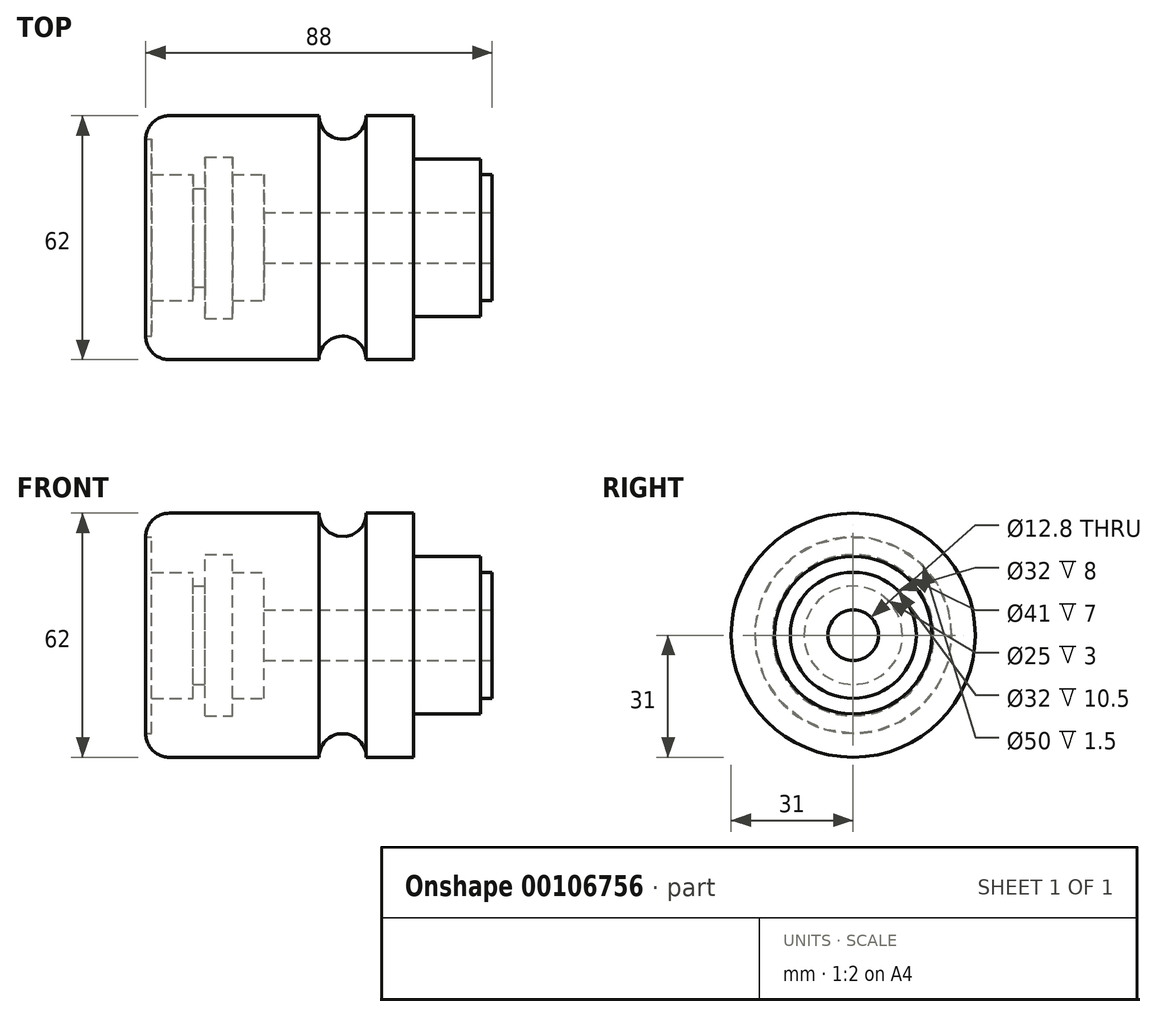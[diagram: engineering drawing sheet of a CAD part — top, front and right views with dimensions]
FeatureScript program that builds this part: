
annotation { "Feature Type Name" : "Feature", "Feature Type Description" : "" }
export const myFeature = defineFeature(function(context is Context, id is Id, definition is map)
    precondition{}
    {
        {
            var Q0;
            Q0=qCreatedBy(makeId("Front.planeOp"),FACE);
            var sketch = newSketch(context, id + "F0", { "sketchPlane" : qUnion([Q0])});
            skLineSegment(sketch, "E0", {"start": v(0, 0) * mm, "end": v(88, 0) * mm, "construction": true});
            skLineSegment(sketch, "E1.bottom", {"start": v(88, 0) * mm, "end": v(85, 0) * mm});
            skLineSegment(sketch, "E1.top", {"start": v(88, 16) * mm, "end": v(85, 16) * mm});
            skLineSegment(sketch, "E1.left", {"start": v(88, 0) * mm, "end": v(88, 16) * mm});
            skLineSegment(sketch, "E1.right", {"start": v(85, 0) * mm, "end": v(85, 16) * mm});
            skLineSegment(sketch, "E2.bottom", {"start": v(85, 0) * mm, "end": v(68, 0) * mm});
            skLineSegment(sketch, "E2.top", {"start": v(85, 20) * mm, "end": v(68, 20) * mm});
            skLineSegment(sketch, "E2.left", {"start": v(85, 0) * mm, "end": v(85, 20) * mm});
            skLineSegment(sketch, "E2.right", {"start": v(68, 0) * mm, "end": v(68, 20) * mm});
            skLineSegment(sketch, "E3.bottom", {"start": v(68, 0) * mm, "end": v(56, 0) * mm});
            skLineSegment(sketch, "E3.top", {"start": v(68, 31) * mm, "end": v(56, 31) * mm});
            skLineSegment(sketch, "E3.left", {"start": v(68, 0) * mm, "end": v(68, 31) * mm});
            skLineSegment(sketch, "E3.right", {"start": v(56, 0) * mm, "end": v(56, 31) * mm});
            skLineSegment(sketch, "E4.bottom", {"start": v(56, 0) * mm, "end": v(0, 0) * mm});
            skLineSegment(sketch, "E4.top", {"start": v(56, 31) * mm, "end": v(6, 31) * mm});
            skLineSegment(sketch, "E4.right", {"start": v(0, 0) * mm, "end": v(0, 25) * mm});
            skPoint(sketch, "E5.visualSharp", {"position": v(0, 31) * mm});
            skArc(sketch, "E5.filletArc", {"start": v(6, 31) * mm, "mid": v(1.76, 29.24) * mm, "end": v(0, 25) * mm});
            skLineSegment(sketch, "E6", {"start": v(44, 31) * mm, "end": v(44, 0) * mm});
            skArc(sketch, "E7", {"start": v(44, 31) * mm, "mid": v(50, 25) * mm, "end": v(56, 31) * mm});
            skSolve(sketch);
        }
        {
            var Q0;
            {var subQ1=sQuery(id+"F0.wireOp",EDGE,"E4.right");Q0=makeQuery(id+"F0.imprint","IMPRINT",FACE,{"disambiguationData":[TD([[makeQuery(id+"F0.imprint","IMPRINT",EDGE,{"derivedFrom":subQ1}),-1.0]])]});}
            var Q1;
            {var subQ0=sQuery(id+"F0.wireOp",EDGE,"E3.right");Q1=makeQuery(id+"F0.imprint","IMPRINT",FACE,{"disambiguationData":[TD([[makeQuery(id+"F0.imprint","IMPRINT",EDGE,{"derivedFrom":subQ0}),1.0]])]});}
            var Q2;
            {var subQ3=sQuery(id+"F0.wireOp",EDGE,"E3.bottom");Q2=makeQuery(id+"F0.imprint","IMPRINT",FACE,{"disambiguationData":[TD([[makeQuery(id+"F0.imprint","IMPRINT",EDGE,{"derivedFrom":subQ3}),-1.0]])]});}
            var Q3;
            {var subQ3=sQuery(id+"F0.wireOp",EDGE,"E2.bottom");Q3=makeQuery(id+"F0.imprint","IMPRINT",FACE,{"disambiguationData":[TD([[makeQuery(id+"F0.imprint","IMPRINT",EDGE,{"derivedFrom":subQ3}),-1.0]])]});}
            var Q4;
            {var subQ0=sQuery(id+"F0.wireOp",EDGE,"E1.bottom");Q4=makeQuery(id+"F0.imprint","IMPRINT",FACE,{"disambiguationData":[TD([[makeQuery(id+"F0.imprint","IMPRINT",EDGE,{"derivedFrom":subQ0}),-1.0]])]});}
            var Q5;
            Q5=sQuery(id+"F0.wireOp",EDGE,"E4.bottom");
            revolve(context, id + "F1", {"entities" : qUnion([Q0, Q1, Q2, Q3, Q4]), "axis" : qUnion([Q5]), "revolveType" : RevolveType.FULL});
        }
        {
            var Q0;
            Q0=qCreatedBy(makeId("Front.planeOp"),FACE);
            var sketch = newSketch(context, id + "F2", { "sketchPlane" : qUnion([Q0])});
            skLineSegment(sketch, "E8", {"start": v(0, 0) * mm, "end": v(149.16, 0) * mm, "construction": true});
            skLineSegment(sketch, "E9.bottom", {"start": v(88, 0) * mm, "end": v(30, 0) * mm});
            skLineSegment(sketch, "E9.top", {"start": v(88, 6.4) * mm, "end": v(30, 6.4) * mm});
            skLineSegment(sketch, "E9.left", {"start": v(88, 0) * mm, "end": v(88, 6.4) * mm});
            skLineSegment(sketch, "E9.right", {"start": v(30, 0) * mm, "end": v(30, 6.4) * mm});
            skLineSegment(sketch, "E10.bottom", {"start": v(30, 0) * mm, "end": v(22, 0) * mm});
            skLineSegment(sketch, "E10.top", {"start": v(30, 16) * mm, "end": v(22, 16) * mm});
            skLineSegment(sketch, "E10.left", {"start": v(30, 0) * mm, "end": v(30, 16) * mm});
            skLineSegment(sketch, "E10.right", {"start": v(22, 0) * mm, "end": v(22, 16) * mm});
            skLineSegment(sketch, "E11.bottom", {"start": v(22, 0) * mm, "end": v(15, 0) * mm});
            skLineSegment(sketch, "E11.top", {"start": v(22, 20.5) * mm, "end": v(15, 20.5) * mm});
            skLineSegment(sketch, "E11.left", {"start": v(22, 0) * mm, "end": v(22, 20.5) * mm});
            skLineSegment(sketch, "E11.right", {"start": v(15, 0) * mm, "end": v(15, 20.5) * mm});
            skLineSegment(sketch, "E12.bottom", {"start": v(15, 0) * mm, "end": v(12, 0) * mm});
            skLineSegment(sketch, "E12.top", {"start": v(15, 12.5) * mm, "end": v(12, 12.5) * mm});
            skLineSegment(sketch, "E12.left", {"start": v(15, 0) * mm, "end": v(15, 12.5) * mm});
            skLineSegment(sketch, "E12.right", {"start": v(12, 0) * mm, "end": v(12, 12.5) * mm});
            skLineSegment(sketch, "E13.bottom", {"start": v(12, 0) * mm, "end": v(1.5, 0) * mm});
            skLineSegment(sketch, "E13.top", {"start": v(12, 16) * mm, "end": v(1.5, 16) * mm});
            skLineSegment(sketch, "E13.left", {"start": v(12, 0) * mm, "end": v(12, 16) * mm});
            skLineSegment(sketch, "E13.right", {"start": v(1.5, 0) * mm, "end": v(1.5, 16) * mm});
            skLineSegment(sketch, "E14.bottom", {"start": v(0, 0) * mm, "end": v(1.5, 0) * mm});
            skLineSegment(sketch, "E14.top", {"start": v(0, 0) * mm, "end": v(1.5, 0) * mm});
            skLineSegment(sketch, "E14.left", {"start": v(0, 0) * mm, "end": v(0, 0) * mm});
            skLineSegment(sketch, "E14.right", {"start": v(1.5, 0) * mm, "end": v(1.5, 0) * mm});
            skLineSegment(sketch, "E15.bottom", {"start": v(1.5, 0) * mm, "end": v(0, 0) * mm});
            skLineSegment(sketch, "E15.top", {"start": v(1.5, 25) * mm, "end": v(0, 25) * mm});
            skLineSegment(sketch, "E15.left", {"start": v(1.5, 0) * mm, "end": v(1.5, 25) * mm});
            skLineSegment(sketch, "E15.right", {"start": v(0, 0) * mm, "end": v(0, 25) * mm});
            skSolve(sketch);
        }
        {
            var Q0;
            Q0 = qSketchRegion(id + "F2", true);
            var Q1;
            Q1=sQuery(id+"F2.wireOp",EDGE,"E8");
            revolve(context, id + "F3", {"operationType" : NewBodyOperationType.REMOVE, "entities" : qUnion([Q0]), "axis" : qUnion([Q1]), "revolveType" : RevolveType.FULL, "oppositeDirection" : true});
        }
    });
